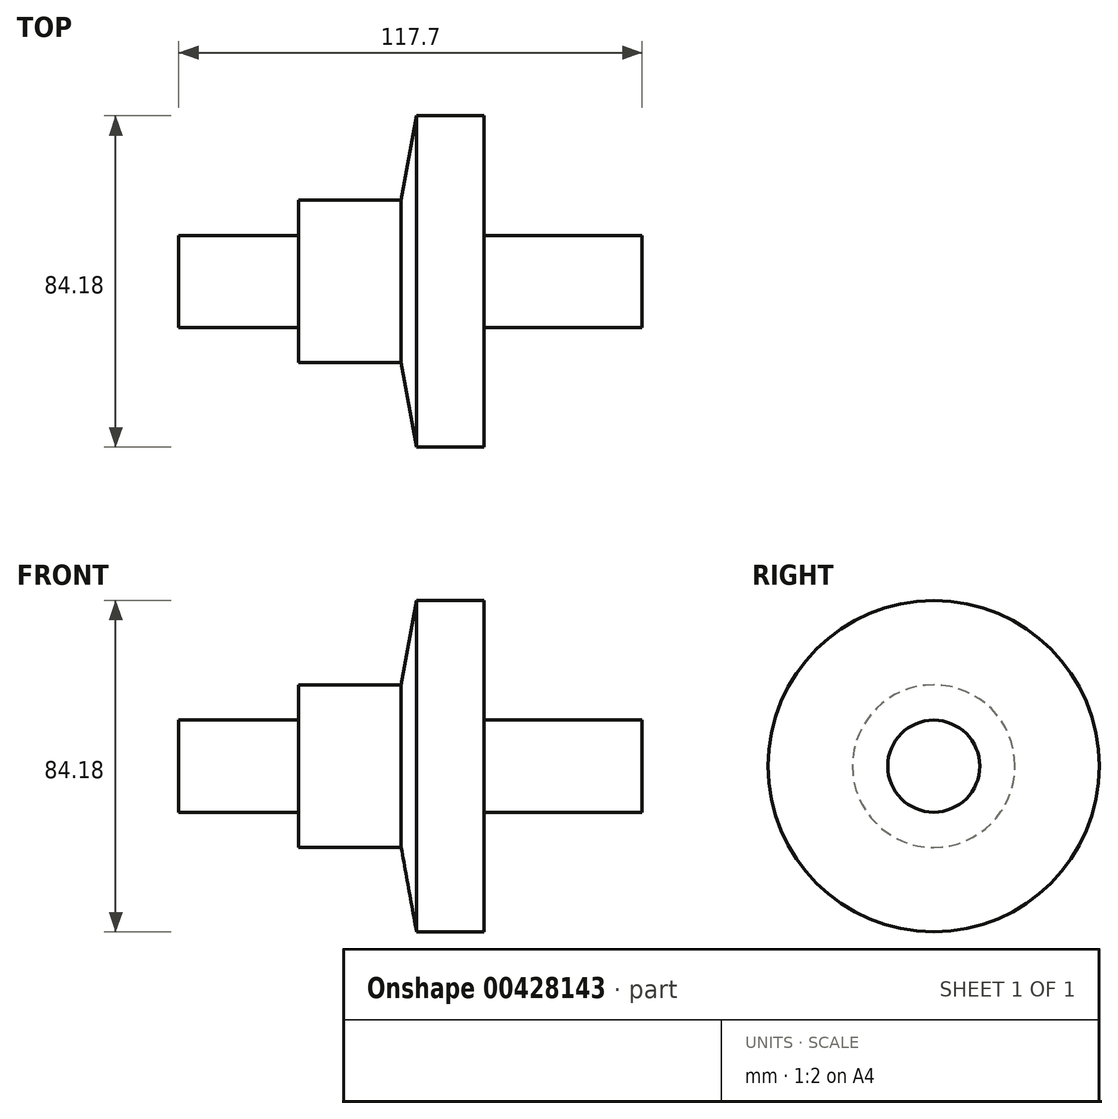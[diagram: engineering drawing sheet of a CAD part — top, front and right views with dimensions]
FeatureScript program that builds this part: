
annotation { "Feature Type Name" : "Feature", "Feature Type Description" : "" }
export const myFeature = defineFeature(function(context is Context, id is Id, definition is map)
    precondition{}
    {
        {
            var Q0;
            Q0=qCreatedBy(makeId("Front.planeOp"),FACE);
            var sketch = newSketch(context, id + "F0", { "sketchPlane" : qUnion([Q0])});
            skLineSegment(sketch, "E0", {"start": v(-69.76, 0) * mm, "end": v(-69.76, 11.7) * mm});
            skLineSegment(sketch, "E1", {"start": v(-69.76, 11.7) * mm, "end": v(-39.36, 11.7) * mm});
            skLineSegment(sketch, "E2", {"start": v(-39.36, 11.7) * mm, "end": v(-39.36, 20.66) * mm});
            skLineSegment(sketch, "E3", {"start": v(-39.36, 20.66) * mm, "end": v(-13.25, 20.66) * mm});
            skLineSegment(sketch, "E4", {"start": v(-13.25, 20.66) * mm, "end": v(-9.35, 42.1) * mm});
            skLineSegment(sketch, "E5", {"start": v(-9.35, 42.1) * mm, "end": v(7.8, 42.1) * mm});
            skLineSegment(sketch, "E6", {"start": v(7.8, 42.1) * mm, "end": v(7.8, 11.7) * mm});
            skLineSegment(sketch, "E7", {"start": v(7.8, 11.7) * mm, "end": v(47.94, 11.7) * mm});
            skLineSegment(sketch, "E8", {"start": v(47.94, 11.7) * mm, "end": v(47.94, 0) * mm});
            skLineSegment(sketch, "E9", {"start": v(47.94, 0) * mm, "end": v(-69.76, 0) * mm});
            skSolve(sketch);
        }
        {
            var Q0;
            Q0=makeQuery(id+"F0.imprint","IMPRINT",FACE,{"disambiguationData":[TD([[makeQuery(id+"F0.imprint","IMPRINT",EDGE,{"derivedFrom":sQuery(id+"F0.wireOp",EDGE,"E0")}),-1.0]])]});
            var Q1;
            Q1=sQuery(id+"F0.wireOp",EDGE,"E9");
            revolve(context, id + "F1", {"entities" : qUnion([Q0]), "axis" : qUnion([Q1]), "revolveType" : RevolveType.FULL});
        }
    });
